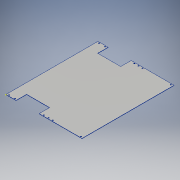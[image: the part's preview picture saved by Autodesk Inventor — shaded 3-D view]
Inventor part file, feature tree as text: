
AUTODESK INVENTOR PART (.ipt)
format: ipt  version: 2018 (Build 220112000, 112)  size: 151,040 bytes
history: native  units: in
note: dims shown in document units (in); Inventor stores cm internally (conversion verified against a paired STEP export)
features: sketch x3, extrude x2
ambient origin geometry x8: Origin, YZ Plane, XZ Plane, XY Plane, X Axis, Y Axis, Z Axis, Center Point
bodies: Solid1 (feature_tree)
feature tree (5):
  sketch  "Sketch1"  dims[d1=22.0in d2=5.5in]
  extrude  "Extrusion1"  Depth=5.5in
  extrude  "Extrusion2"  Depth=2.5in
  sketch  "Sketch2"  dims[d3=2.438in d4=2.5in]
  sketch  "Sketch3"  dims[d5=0.0625in d6=0.0in d8=10.25in d9=0.5in d10=0.5in d11=0.5in d12=1.0in d13=1.0in d14=1.0in d15=0.5in d16=0.5in d17=0.256in d18=0.5in d19=7.0in d20=7.0in d21=0.256in d22=1.0in d23=0.0in]
